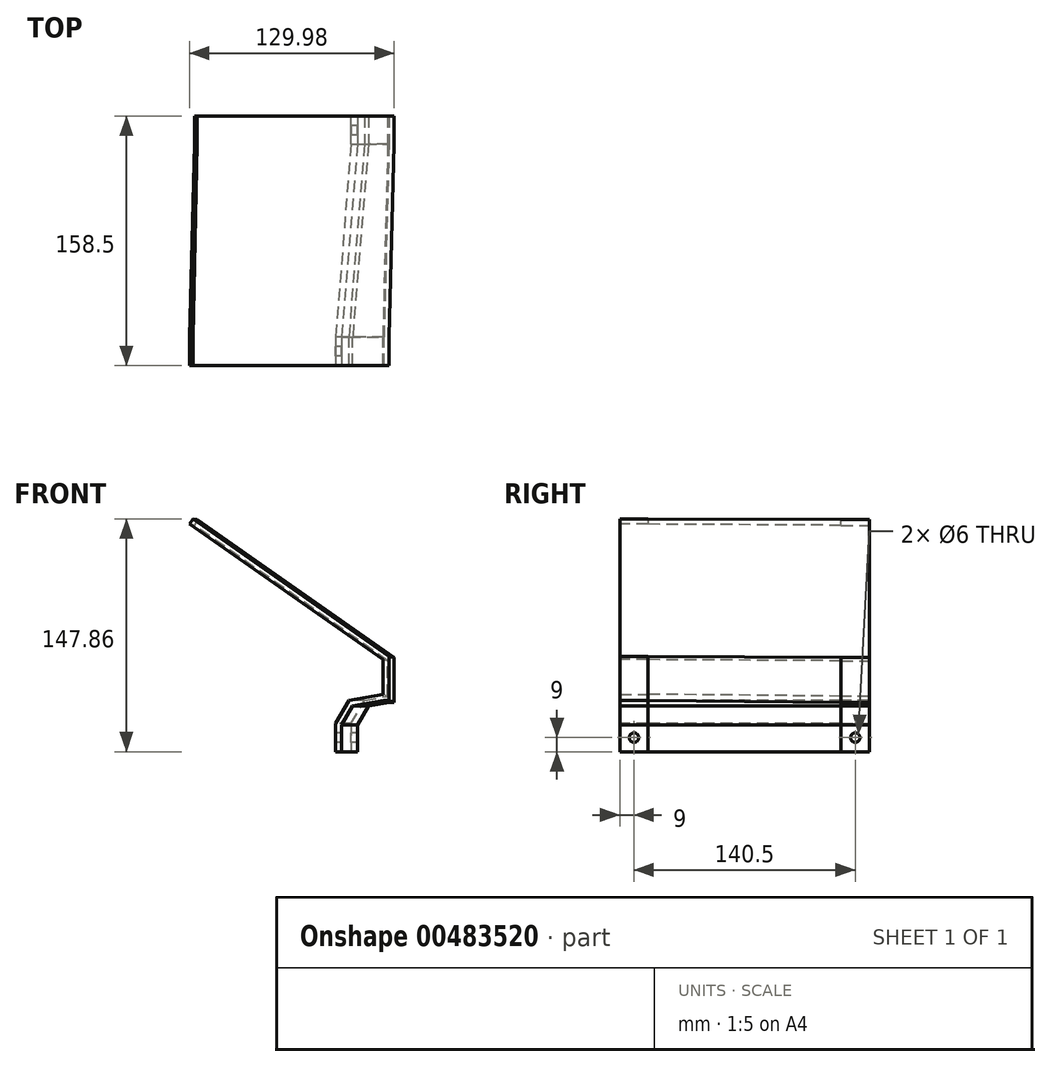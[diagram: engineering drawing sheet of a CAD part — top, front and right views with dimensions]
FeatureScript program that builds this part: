
annotation { "Feature Type Name" : "Feature", "Feature Type Description" : "" }
export const myFeature = defineFeature(function(context is Context, id is Id, definition is map)
    precondition{}
    {
        {
            var Q0;
            Q0=qCreatedBy(makeId("Right.planeOp"),FACE);
            cPlane(context, id + "F0", {"entities" : qUnion([Q0]), "cplaneType" : CPlaneType.OFFSET, "offset" : 10 * mm, "oppositeDirection" : true, "width" : 152.4 * mm, "height" : 152.4 * mm});
        }
        {
            var Q0;
            Q0=qCreatedBy(makeId("Front.planeOp"),FACE);
            cPlane(context, id + "F1", {"entities" : qUnion([Q0]), "cplaneType" : CPlaneType.OFFSET, "offset" : (140.5 / 2) * mm, "width" : 150 * mm, "height" : 150 * mm});
        }
        {
            var Q0;
            Q0=qCreatedBy(makeId("Front.planeOp"),FACE);
            cPlane(context, id + "F2", {"entities" : qUnion([Q0]), "cplaneType" : CPlaneType.OFFSET, "offset" : (140.5 / 2) * mm, "oppositeDirection" : true, "width" : 150 * mm, "height" : 150 * mm});
        }
        {
            var Q0;
            Q0=qCreatedBy(makeId("Right.planeOp"),FACE);
            var sketch = newSketch(context, id + "F3", { "sketchPlane" : qUnion([Q0])});
            skLineSegment(sketch, "E0.bottom", {"start": v(61.25, 9) * mm, "end": v(79.25, 9) * mm});
            skLineSegment(sketch, "E0.top", {"start": v(61.25, -9) * mm, "end": v(79.25, -9) * mm});
            skLineSegment(sketch, "E0.left", {"start": v(61.25, 9) * mm, "end": v(61.25, -9) * mm});
            skLineSegment(sketch, "E0.right", {"start": v(79.25, 9) * mm, "end": v(79.25, -9) * mm});
            skLineSegment(sketch, "E1", {"start": v(61.25, 0) * mm, "end": v(0, 0) * mm, "construction": true});
            skLineSegment(sketch, "E2", {"start": v(70.25, 9) * mm, "end": v(70.25, 29.54) * mm, "construction": true});
            skLineSegment(sketch, "E3", {"start": v(79.25, 9) * mm, "end": v(61.25, -9) * mm, "construction": true});
            skCircle(sketch, "E4", {"center": v(70.25, 0) * mm, "radius": 3 * mm});
            skSolve(sketch);
        }
        {
            var Q0;
            Q0 = qSketchRegion(id + "F3", true);
            extrude(context, id + "F4", {"entities" : qUnion([Q0]), "endBound" : BoundingType.SYMMETRIC, "depth" : 4 * mm});
        }
        {
            var Q0;
            Q0=qCreatedBy(id+"F0.planeOp",FACE);
            var sketch = newSketch(context, id + "F5", { "sketchPlane" : qUnion([Q0])});
            skLineSegment(sketch, "E5", {"start": v(0, 0) * mm, "end": v(-61.25, 0) * mm, "construction": true});
            skLineSegment(sketch, "E6", {"start": v(-70.25, 9) * mm, "end": v(-70.25, 30.02) * mm, "construction": true});
            skLineSegment(sketch, "E7.bottom", {"start": v(-61.25, 9) * mm, "end": v(-79.25, 9) * mm});
            skLineSegment(sketch, "E7.top", {"start": v(-61.25, -9) * mm, "end": v(-79.25, -9) * mm});
            skLineSegment(sketch, "E7.left", {"start": v(-61.25, 9) * mm, "end": v(-61.25, -9) * mm});
            skLineSegment(sketch, "E7.right", {"start": v(-79.25, 9) * mm, "end": v(-79.25, -9) * mm});
            skLineSegment(sketch, "E8", {"start": v(-61.25, 9) * mm, "end": v(-79.25, -9) * mm, "construction": true});
            skCircle(sketch, "E9", {"center": v(-70.25, 0) * mm, "radius": 3 * mm});
            skSolve(sketch);
        }
        {
            var Q0;
            Q0 = qSketchRegion(id + "F5", true);
            extrude(context, id + "F6", {"entities" : qUnion([Q0]), "endBound" : BoundingType.SYMMETRIC, "depth" : 4 * mm});
        }
        {
            var Q0;
            Q0=qCreatedBy(id+"F2.planeOp",FACE);
            var sketch = newSketch(context, id + "F7", { "sketchPlane" : qUnion([Q0])});
            skLineSegment(sketch, "E10", {"start": v(-2, 9) * mm, "end": v(6.5, 23.72) * mm});
            skLineSegment(sketch, "E11", {"start": v(-2, 9) * mm, "end": v(2, 9) * mm});
            skLineSegment(sketch, "E12", {"start": v(6.5, 23.72) * mm, "end": v(21.27, 26.33) * mm});
            skLineSegment(sketch, "E13", {"start": v(21.27, 26.33) * mm, "end": v(21.97, 22.39) * mm});
            skLineSegment(sketch, "E14", {"start": v(21.97, 22.39) * mm, "end": v(9.03, 20.1) * mm});
            skLineSegment(sketch, "E15", {"start": v(2, 9) * mm, "end": v(2, 7.93) * mm});
            skLineSegment(sketch, "E16", {"start": v(2, 7.93) * mm, "end": v(9.03, 20.1) * mm});
            skSolve(sketch);
        }
        {
            var Q0;
            Q0 = qSketchRegion(id + "F7", true);
            var Q1;
            Q1=makeQuery(id+"F4.opExtrude","CAP_VERTEX",VERTEX,{"disambiguationData":[OSD([sQuery(id+"F3.wireOp",EDGE,"E0.bottom"),sQuery(id+"F3.wireOp",EDGE,"E0.right")])],"isStart":false});
            var Q2;
            Q2=makeQuery(id+"F4.opExtrude","CAP_VERTEX",VERTEX,{"disambiguationData":[OSD([sQuery(id+"F3.wireOp",EDGE,"E0.bottom"),sQuery(id+"F3.wireOp",EDGE,"E0.left")])],"isStart":false});
            extrude(context, id + "F8", {"entities" : qUnion([Q0]), "operationType" : NewBodyOperationType.ADD, "endBound" : BoundingType.UP_TO_VERTEX, "oppositeDirection" : true, "endBoundEntityVertex" : qUnion([Q1]), "depth" : 25 * mm, "hasSecondDirection" : true, "secondDirectionBound" : SecondDirectionBoundingType.UP_TO_VERTEX, "secondDirectionOppositeDirection" : false, "secondDirectionBoundEntityVertex" : qUnion([Q2]), "secondDirectionDepth" : 15 * mm});
        }
        {
            var Q0;
            Q0=qCreatedBy(id+"F1.planeOp",FACE);
            var sketch = newSketch(context, id + "F9", { "sketchPlane" : qUnion([Q0])});
            skLineSegment(sketch, "E17", {"start": v(-3.5, 23.72) * mm, "end": v(-12, 9) * mm});
            skLineSegment(sketch, "E18", {"start": v(-12, 9) * mm, "end": v(-8, 9) * mm});
            skLineSegment(sketch, "E19", {"start": v(-8, 9) * mm, "end": v(-8, 7.93) * mm});
            skLineSegment(sketch, "E20", {"start": v(-8, 7.93) * mm, "end": v(-0.97, 20.1) * mm});
            skLineSegment(sketch, "E21", {"start": v(-3.5, 23.72) * mm, "end": v(18.17, 27.54) * mm});
            skLineSegment(sketch, "E22", {"start": v(18.17, 27.54) * mm, "end": v(18.86, 23.6) * mm});
            skLineSegment(sketch, "E23", {"start": v(18.86, 23.6) * mm, "end": v(-0.97, 20.1) * mm});
            skSolve(sketch);
        }
        {
            var Q0;
            Q0 = qSketchRegion(id + "F9", true);
            var Q1;
            Q1=makeQuery(id+"F6.opExtrude","CAP_VERTEX",VERTEX,{"disambiguationData":[OSD([sQuery(id+"F5.wireOp",EDGE,"E7.bottom"),sQuery(id+"F5.wireOp",EDGE,"E7.right")])],"isStart":false});
            var Q2;
            Q2=makeQuery(id+"F6.opExtrude","CAP_VERTEX",VERTEX,{"disambiguationData":[OSD([sQuery(id+"F5.wireOp",EDGE,"E7.bottom"),sQuery(id+"F5.wireOp",EDGE,"E7.left")])],"isStart":false});
            extrude(context, id + "F10", {"entities" : qUnion([Q0]), "operationType" : NewBodyOperationType.ADD, "endBound" : BoundingType.UP_TO_VERTEX, "endBoundEntityVertex" : qUnion([Q1]), "depth" : 25 * mm, "hasSecondDirection" : true, "secondDirectionBound" : SecondDirectionBoundingType.UP_TO_VERTEX, "secondDirectionOppositeDirection" : true, "secondDirectionBoundEntityVertex" : qUnion([Q2]), "secondDirectionDepth" : 25 * mm});
        }
        {
            var Q0;
            Q0=makeQuery(id+"F8.boolean.opBoolean","MERGE",FACE,{"derivedFrom":[makeQuery(id+"F4.opExtrude","SWEPT_FACE",FACE,{"disambiguationData":[OSD([sQuery(id+"F3.wireOp",EDGE,"E0.right")])]}),makeQuery(id+"F8.opExtrude","CAP_FACE",FACE,{"disambiguationData":[OSD([dummyQuery(id+"F8.vertexPlane.planeOp",FACE)])],"isStart":false})]});
            var sketch = newSketch(context, id + "F11", { "sketchPlane" : qUnion([Q0])});
            skLineSegment(sketch, "E24", {"start": v(-21.27, 26.33) * mm, "end": v(-21.27, 48.83) * mm});
            skLineSegment(sketch, "E25", {"start": v(-21.27, 48.83) * mm, "end": v(101.6, 134.86) * mm});
            skLineSegment(sketch, "E26", {"start": v(-21.27, 26.33) * mm, "end": v(-21.97, 22.39) * mm});
            skLineSegment(sketch, "E27", {"start": v(-21.97, 22.39) * mm, "end": v(-25.27, 22.39) * mm});
            skLineSegment(sketch, "E28", {"start": v(-25.27, 22.39) * mm, "end": v(-25.27, 50.9) * mm});
            skLineSegment(sketch, "E29", {"start": v(-25.27, 50.9) * mm, "end": v(99.8, 138.48) * mm});
            skLineSegment(sketch, "E30", {"start": v(99.8, 138.48) * mm, "end": v(101.6, 134.86) * mm});
            skSolve(sketch);
        }
        {
            var Q0;
            Q0 = qSketchRegion(id + "F11", true);
            var Q1;
            Q1=makeQuery(id+"F8.boolean.opBoolean","MERGE",FACE,{"derivedFrom":[makeQuery(id+"F4.opExtrude","SWEPT_FACE",FACE,{"disambiguationData":[OSD([sQuery(id+"F3.wireOp",EDGE,"E0.left")])]}),makeQuery(id+"F8.opExtrude","CAP_FACE",FACE,{"disambiguationData":[OSD([dummyQuery(id+"F8.secondVertexPlane.planeOp",FACE)])],"isStart":true})]});
            extrude(context, id + "F12", {"entities" : qUnion([Q0]), "operationType" : NewBodyOperationType.ADD, "endBound" : BoundingType.UP_TO_SURFACE, "oppositeDirection" : true, "depth" : 25 * mm, "endBoundEntityFace" : qUnion([Q1]), "offsetDistance" : 25 * mm});
        }
        {
            var Q0;
            Q0=makeQuery(id+"F10.boolean.opBoolean","MERGE",FACE,{"derivedFrom":[makeQuery(id+"F6.opExtrude","SWEPT_FACE",FACE,{"disambiguationData":[OSD([sQuery(id+"F5.wireOp",EDGE,"E7.right")])]}),makeQuery(id+"F10.opExtrude","CAP_FACE",FACE,{"disambiguationData":[OSD([dummyQuery(id+"F10.vertexPlane.planeOp",FACE)])],"isStart":false})]});
            var sketch = newSketch(context, id + "F13", { "sketchPlane" : qUnion([Q0])});
            skLineSegment(sketch, "E31", {"start": v(18.17, 27.54) * mm, "end": v(18.17, 49.54) * mm});
            skLineSegment(sketch, "E32", {"start": v(18.17, 49.54) * mm, "end": v(-104.7, 135.58) * mm});
            skLineSegment(sketch, "E33.0", {"start": v(22.17, 51.62) * mm, "end": v(-102.41, 138.86) * mm});
            skLineSegment(sketch, "E33.1", {"start": v(22.17, 23.6) * mm, "end": v(22.17, 51.62) * mm});
            skLineSegment(sketch, "E34", {"start": v(-102.41, 138.86) * mm, "end": v(-104.7, 135.58) * mm});
            skLineSegment(sketch, "E35", {"start": v(18.86, 23.6) * mm, "end": v(22.17, 23.6) * mm});
            skLineSegment(sketch, "E36", {"start": v(18.17, 27.54) * mm, "end": v(18.86, 23.6) * mm});
            skSolve(sketch);
        }
        {
            var Q0;
            Q0 = qSketchRegion(id + "F13", true);
            var Q1;
            Q1=makeQuery(id+"F10.boolean.opBoolean","MERGE",FACE,{"derivedFrom":[makeQuery(id+"F6.opExtrude","SWEPT_FACE",FACE,{"disambiguationData":[OSD([sQuery(id+"F5.wireOp",EDGE,"E7.left")])]}),makeQuery(id+"F10.opExtrude","CAP_FACE",FACE,{"disambiguationData":[OSD([dummyQuery(id+"F10.secondVertexPlane.planeOp",FACE)])],"isStart":true})]});
            extrude(context, id + "F14", {"entities" : qUnion([Q0]), "operationType" : NewBodyOperationType.ADD, "endBound" : BoundingType.UP_TO_SURFACE, "oppositeDirection" : true, "depth" : 25 * mm, "endBoundEntityFace" : qUnion([Q1]), "offsetDistance" : 25 * mm});
        }
        {
            var Q0;
            {var subQ0=dummyQuery(id+"F8.secondVertexPlane.planeOp",FACE);var subQ1=sQuery(id+"F3.wireOp",EDGE,"E0.left");Q0=makeQuery(id+"F12.boolean.opBoolean","MERGE",FACE,{"derivedFrom":[makeQuery(id+"F8.boolean.opBoolean","MERGE",FACE,{"derivedFrom":[makeQuery(id+"F4.opExtrude","SWEPT_FACE",FACE,{"disambiguationData":[OSD([subQ1])]}),makeQuery(id+"F8.opExtrude","CAP_FACE",FACE,{"disambiguationData":[OSD([subQ0])],"isStart":true})]}),makeQuery(id+"F12.opExtrude","CAP_FACE",FACE,{"disambiguationData":[OSD([subQ1,subQ0])],"isStart":false})]});}
            var Q1;
            {var subQ0=dummyQuery(id+"F10.secondVertexPlane.planeOp",FACE);var subQ1=sQuery(id+"F5.wireOp",EDGE,"E7.left");Q1=makeQuery(id+"F14.boolean.opBoolean","MERGE",FACE,{"derivedFrom":[makeQuery(id+"F10.boolean.opBoolean","MERGE",FACE,{"derivedFrom":[makeQuery(id+"F6.opExtrude","SWEPT_FACE",FACE,{"disambiguationData":[OSD([subQ1])]}),makeQuery(id+"F10.opExtrude","CAP_FACE",FACE,{"disambiguationData":[OSD([subQ0])],"isStart":true})]}),makeQuery(id+"F14.opExtrude","CAP_FACE",FACE,{"disambiguationData":[OSD([subQ1,subQ0])],"isStart":false})]});}
            loft(context, id + "F15", {"operationType" : NewBodyOperationType.ADD, "sheetProfilesArray" : [{ "sheetProfileEntities" : qUnion([Q0]) }, { "sheetProfileEntities" : qUnion([Q1]) }]});
        }
    });
